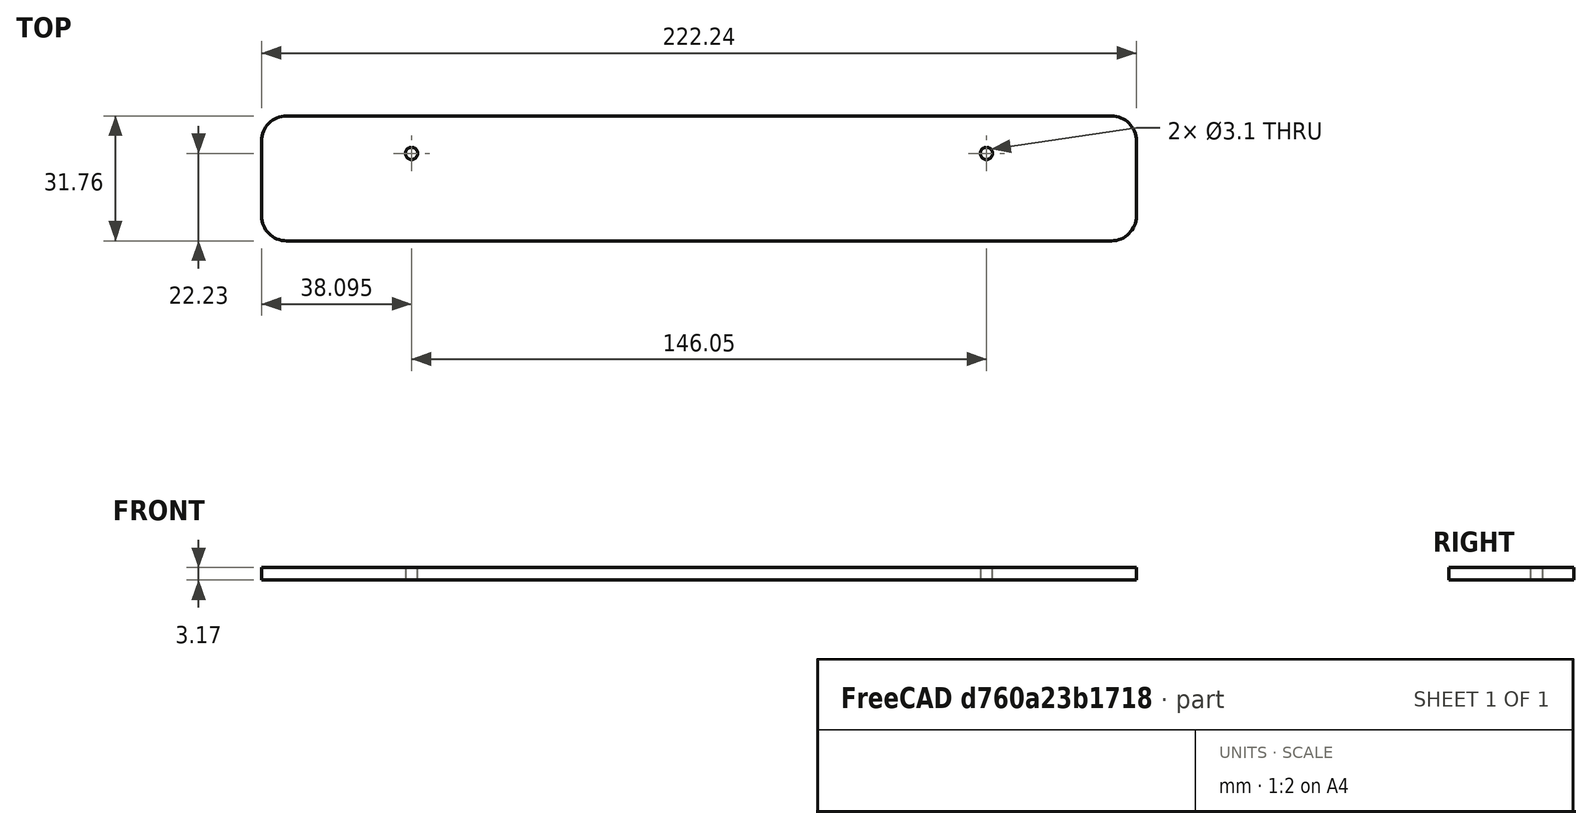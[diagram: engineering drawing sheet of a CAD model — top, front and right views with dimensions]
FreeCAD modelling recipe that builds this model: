
FCSTD DOCUMENT  (FreeCAD 0.19R22756 (Git))
Label: X22_Foot1
License: All rights reserved
LicenseURL: http://en.wikipedia.org/wiki/All_rights_reserved
objects: Sketcher::SketchObject×1, PartDesign::Pad×1, PartDesign::Body×1, PartDesign::CoordinateSystem×1, App::Part×1
note: 5 computed .brp shape members not serialized (recipe doc carries the construction recipe); baked Part::Feature solids carry a one-line shape summary decoded from their .brp

FEATURE [Sketcher::SketchObject] Sketch
  MapMode = 5
  Support = -> [XY_Plane]
  sketch-geometry (11):
    g0: LineSegment StartX=-104.775 StartY=15.875 StartZ=0 EndX=104.775 EndY=15.875 EndZ=0
    g1: LineSegment StartX=111.125 StartY=9.525 StartZ=0 EndX=111.125 EndY=-9.525 EndZ=0
    g2: LineSegment StartX=104.775 StartY=-15.875 StartZ=0 EndX=-104.775 EndY=-15.875 EndZ=0
    g3: LineSegment StartX=-111.125 StartY=-9.525 StartZ=0 EndX=-111.125 EndY=9.525 EndZ=0
    g4: ArcOfCircle CenterX=-104.775 CenterY=9.525 CenterZ=0 NormalX=0 NormalY=0 NormalZ=1 AngleXU=0 Radius=6.35 StartAngle=1.5708 EndAngle=3.14159
    g5: ArcOfCircle CenterX=-104.775 CenterY=-9.525 CenterZ=0 NormalX=0 NormalY=0 NormalZ=1 AngleXU=0 Radius=6.35 StartAngle=3.14159 EndAngle=4.71239
    g6: ArcOfCircle CenterX=104.775 CenterY=-9.525 CenterZ=0 NormalX=0 NormalY=0 NormalZ=1 AngleXU=0 Radius=6.35 StartAngle=4.71239 EndAngle=6.28319
    g7: ArcOfCircle CenterX=104.775 CenterY=9.525 CenterZ=0 NormalX=0 NormalY=0 NormalZ=1 AngleXU=0 Radius=6.35 StartAngle=0 EndAngle=1.5708
    g8: Circle CenterX=-73.025 CenterY=6.35 CenterZ=0 NormalX=0 NormalY=0 NormalZ=1 AngleXU=0 Radius=1.55
    g9: Circle CenterX=73.025 CenterY=6.35 CenterZ=0 NormalX=0 NormalY=0 NormalZ=1 AngleXU=0 Radius=1.55
    g10: LineSegment [constr] StartX=0 StartY=0 StartZ=0 EndX=0 EndY=6.35 EndZ=0
  constraints (27):
    c: Horizontal(g0)
    c: Horizontal(g2)
    c: Vertical(g1)
    c: Vertical(g3)
    c: Tangent(g0,g4) = 1.5708
    c: Tangent(g3,g4) = 1.5708
    c: Tangent(g2,g5) = 1.5708
    c: Tangent(g3,g5) = 1.5708
    c: Tangent(g2,g6) = 1.5708
    c: Tangent(g1,g6) = 1.5708
    c: Tangent(g1,g7) = 1.5708
    c: Tangent(g0,g7) = 1.5708
    c: DistanceX(g3,g1) = 222.25
    c: Equal(g4,g5)
    c: Equal(g5,g6)
    c: Equal(g6,g7)
    c: Radius(g4) = 6.35
    c: Symmetric(g4,g6,g-1)
    c: DistanceY(g2,g0) = 31.75
    c: Equal(g8,g9)
    c: DistanceX(g8,g9) = 146.05
    c: Diameter(g8) = 3.1
    c: Coincident(g10,g-1)
    c: PointOnObject(g10,g-2)
    c: DistanceY(g10,g10) = 6.35
    c: Horizontal(g8,g10)
    c: Symmetric(g8,g9,g10)
FEATURE [PartDesign::Pad] Pad
  Direction = (1,1,1)
  Length = 3.175
  Length2 = 99.9998
  Profile = -> Sketch
  Type = 0
FEATURE [PartDesign::Body] Body
  Group = -> [Sketch,Pad]
  Origin = -> Origin
  Tip = -> Pad
FEATURE [PartDesign::CoordinateSystem] LCS_0
  AttacherType = Attacher::AttachEngine3D
  MapMode = 2
  Support = -> [X_Axis001]
FEATURE [App::Part] Part
  Group = -> [LCS_0,Body]
  Origin = -> Origin001
